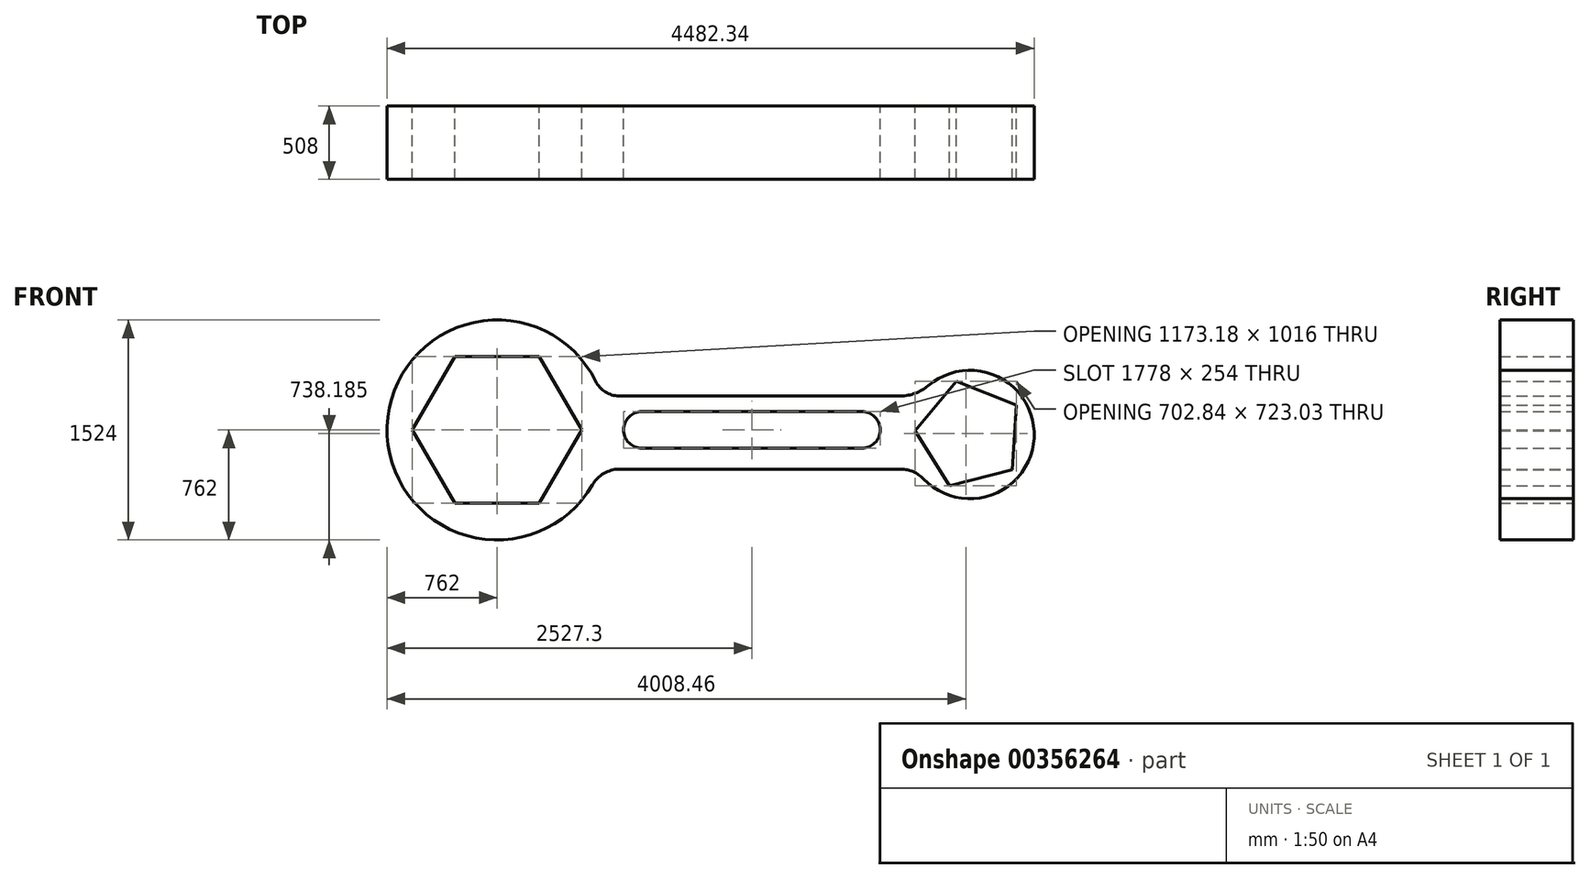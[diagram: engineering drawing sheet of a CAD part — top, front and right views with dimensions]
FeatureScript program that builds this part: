
annotation { "Feature Type Name" : "Feature", "Feature Type Description" : "" }
export const myFeature = defineFeature(function(context is Context, id is Id, definition is map)
    precondition{}
    {
        {
            var Q0;
            Q0=qCreatedBy(makeId("Front.planeOp"),FACE);
            var sketch = newSketch(context, id + "F0", { "sketchPlane" : qUnion([Q0])});
            skCircle(sketch, "E0.cCircle", {"center": v(0, 0) * mm, "radius": 508 * mm, "construction": true});
            skLineSegment(sketch, "E0.0", {"start": v(-293.3, 508) * mm, "end": v(293.3, 508) * mm});
            skLineSegment(sketch, "E0.1", {"start": v(293.3, 508) * mm, "end": v(586.59, 0) * mm});
            skLineSegment(sketch, "E0.2", {"start": v(586.59, 0) * mm, "end": v(293.3, -508) * mm});
            skLineSegment(sketch, "E0.3", {"start": v(293.3, -508) * mm, "end": v(-293.3, -508) * mm});
            skLineSegment(sketch, "E0.4", {"start": v(-293.3, -508) * mm, "end": v(-586.59, 0) * mm});
            skLineSegment(sketch, "E0.5", {"start": v(-586.59, 0) * mm, "end": v(-293.3, 508) * mm});
            skPoint(sketch, "E0.0.midPoint", {"position": v(0, 508) * mm});
            skCircle(sketch, "E1", {"center": v(0, 0) * mm, "radius": 762 * mm});
            skCircle(sketch, "E2", {"center": v(3275.16, -31.8) * mm, "radius": 445.18 * mm});
            skLineSegment(sketch, "E3", {"start": v(845.76, -271.98) * mm, "end": v(2798.79, -271.98) * mm});
            skLineSegment(sketch, "E4", {"start": v(2794.71, 236.02) * mm, "end": v(844.2, 236.02) * mm});
            skLineSegment(sketch, "E5.bottom", {"start": v(1003.3, -127) * mm, "end": v(2527.3, -127) * mm});
            skLineSegment(sketch, "E5.top", {"start": v(1003.3, 127) * mm, "end": v(2527.3, 127) * mm});
            skCircle(sketch, "E6.cCircle", {"center": v(3275.16, -31.8) * mm, "radius": 308.24 * mm, "construction": true});
            skLineSegment(sketch, "E6.0", {"start": v(2895.03, -5.95) * mm, "end": v(3182.28, 337.7) * mm});
            skLineSegment(sketch, "E6.1", {"start": v(3182.28, 337.7) * mm, "end": v(3597.88, 170.7) * mm});
            skLineSegment(sketch, "E6.2", {"start": v(3597.88, 170.7) * mm, "end": v(3567.48, -276.15) * mm});
            skLineSegment(sketch, "E6.3", {"start": v(3567.48, -276.15) * mm, "end": v(3133.1, -385.33) * mm});
            skLineSegment(sketch, "E6.4", {"start": v(3133.1, -385.33) * mm, "end": v(2895.03, -5.95) * mm});
            skPoint(sketch, "E6.0.midPoint", {"position": v(3038.66, 165.88) * mm});
            skArc(sketch, "E7", {"start": v(1003.3, 127) * mm, "mid": v(876.3, 0) * mm, "end": v(1003.3, -127) * mm});
            skArc(sketch, "E8", {"start": v(2527.3, -127) * mm, "mid": v(2654.3, 0) * mm, "end": v(2527.3, 127) * mm});
            skArc(sketch, "E9", {"start": v(684, 335.83) * mm, "mid": v(749.83, 263.02) * mm, "end": v(844.2, 236.02) * mm});
            skArc(sketch, "E10", {"start": v(845.76, -271.98) * mm, "mid": v(739.04, -300.66) * mm, "end": v(661.07, -378.98) * mm});
            skArc(sketch, "E11", {"start": v(2794.71, 236.02) * mm, "mid": v(2896.61, 254.23) * mm, "end": v(2985.9, 306.6) * mm});
            skArc(sketch, "E12", {"start": v(2951.85, -337.85) * mm, "mid": v(2882.1, -289.14) * mm, "end": v(2798.79, -271.98) * mm});
            skSolve(sketch);
        }
        {
            var Q0;
            Q0=makeQuery(id+"F0.imprint","IMPRINT",FACE,{"disambiguationData":[TD([[makeQuery(id+"F0.imprint","IMPRINT",EDGE,{"derivedFrom":sQuery(id+"F0.wireOp",EDGE,"E0.0")}),1.0]])]});
            var Q1;
            Q1=makeQuery(id+"F0.imprint","IMPRINT",FACE,{"disambiguationData":[TD([[makeQuery(id+"F0.imprint","IMPRINT",EDGE,{"derivedFrom":sQuery(id+"F0.wireOp",EDGE,"E3")}),1.0]])]});
            var Q2;
            Q2=makeQuery(id+"F0.imprint","IMPRINT",FACE,{"disambiguationData":[TD([[makeQuery(id+"F0.imprint","IMPRINT",EDGE,{"derivedFrom":sQuery(id+"F0.wireOp",EDGE,"E6.0")}),1.0]])]});
            extrude(context, id + "F1", {"entities" : qUnion([Q0, Q1, Q2]), "depth" : 508 * mm});
        }
    });
